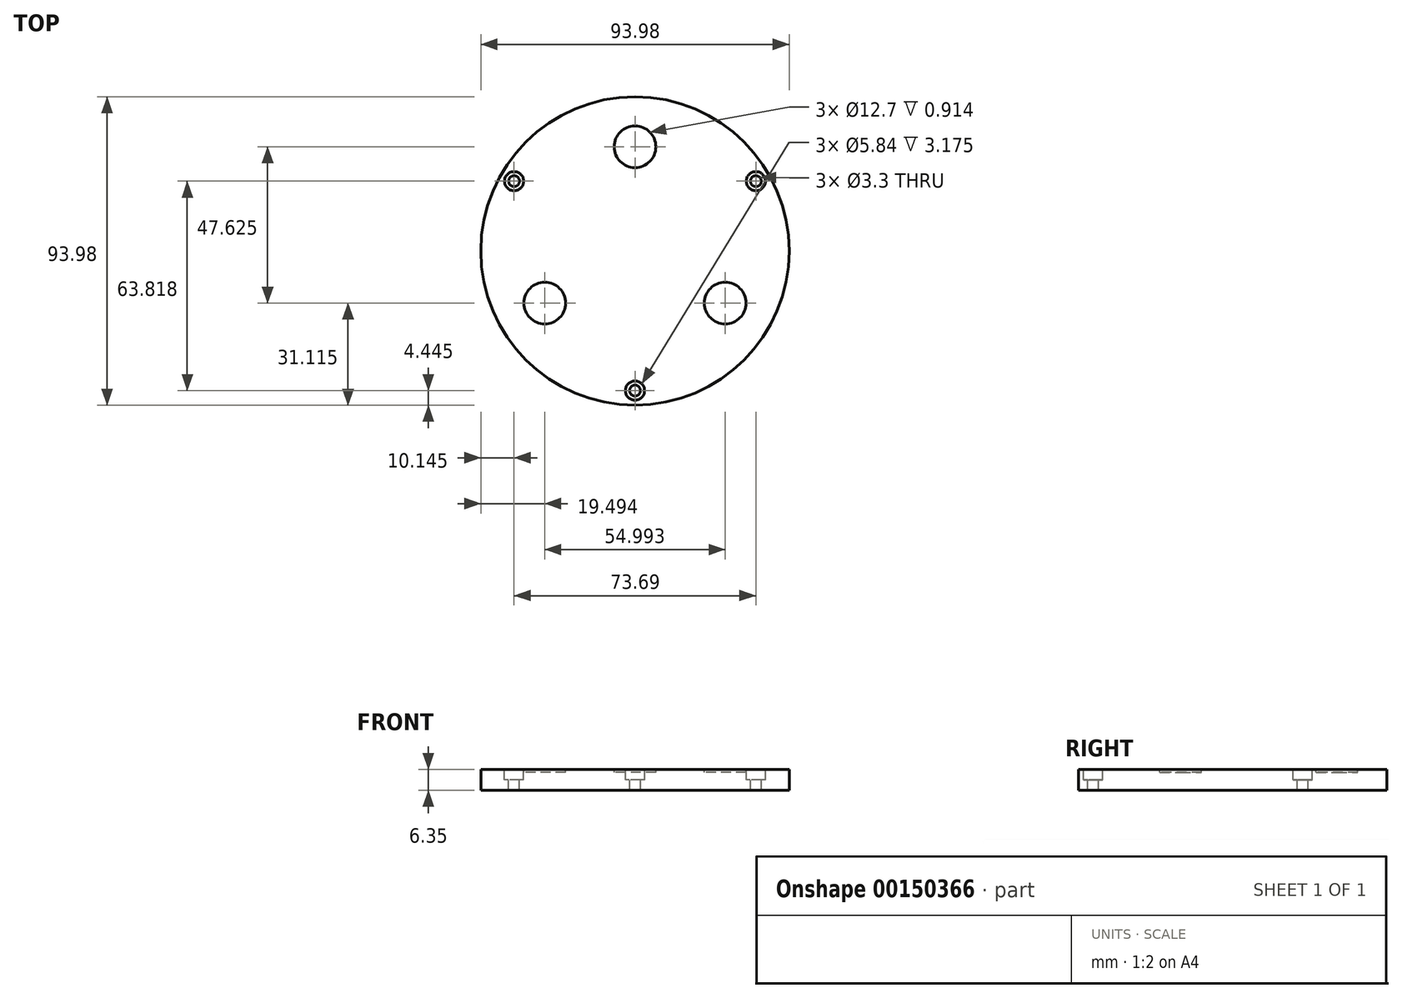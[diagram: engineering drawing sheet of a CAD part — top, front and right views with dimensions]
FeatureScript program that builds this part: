
annotation { "Feature Type Name" : "Feature", "Feature Type Description" : "" }
export const myFeature = defineFeature(function(context is Context, id is Id, definition is map)
    precondition{}
    {
        {
            var Q0;
            Q0=qCreatedBy(makeId("Top.planeOp"),FACE);
            var sketch = newSketch(context, id + "F0", { "sketchPlane" : qUnion([Q0])});
            skCircle(sketch, "E0", {"center": v(0, 0) * mm, "radius": 47 * mm});
            skSolve(sketch);
        }
        {
            var Q0;
            Q0 = qSketchRegion(id + "F0", true);
            extrude(context, id + "F1", {"entities" : qUnion([Q0]), "depth" : 6.35 * mm});
        }
        {
            var Q0;
            Q0=makeQuery(id+"F1.opExtrude","CAP_FACE",FACE,{"disambiguationData":[OSD([sQuery(id+"F0.wireOp",EDGE,"E0")])],"isStart":false});
            var sketch = newSketch(context, id + "F2", { "sketchPlane" : qUnion([Q0])});
            skCircle(sketch, "E1", {"center": v(0, 31.75) * mm, "radius": 6.35 * mm});
            skCircle(sketch, "E2", {"center": v(-27.5, -15.88) * mm, "radius": 6.35 * mm});
            skCircle(sketch, "E3", {"center": v(27.5, -15.88) * mm, "radius": 6.35 * mm});
            skLineSegment(sketch, "E4", {"start": v(0, 31.75) * mm, "end": v(-27.5, -15.88) * mm, "construction": true});
            skLineSegment(sketch, "E5", {"start": v(27.5, -15.88) * mm, "end": v(0, 31.75) * mm, "construction": true});
            skLineSegment(sketch, "E6", {"start": v(27.5, -15.88) * mm, "end": v(-27.5, -15.88) * mm, "construction": true});
            skLineSegment(sketch, "E7", {"start": v(-13.75, 7.94) * mm, "end": v(0, 0) * mm, "construction": true});
            skLineSegment(sketch, "E8", {"start": v(0, 0) * mm, "end": v(0, -15.88) * mm, "construction": true});
            skSolve(sketch);
        }
        {
            var Q0;
            Q0 = qSketchRegion(id + "F2", true);
            extrude(context, id + "F3", {"entities" : qUnion([Q0]), "operationType" : NewBodyOperationType.REMOVE, "oppositeDirection" : true, "depth" : 0.91 * mm});
        }
        {
            var Q0;
            Q0=makeQuery(id+"F1.opExtrude","CAP_FACE",FACE,{"disambiguationData":[OSD([sQuery(id+"F0.wireOp",EDGE,"E0")])],"isStart":false});
            var sketch = newSketch(context, id + "F4", { "sketchPlane" : qUnion([Q0])});
            skCircle(sketch, "E9", {"center": v(0, -42.55) * mm, "radius": 2.92 * mm});
            skCircle(sketch, "E10", {"center": v(-36.85, 21.27) * mm, "radius": 2.92 * mm});
            skCircle(sketch, "E11", {"center": v(36.85, 21.27) * mm, "radius": 2.92 * mm});
            skCircle(sketch, "E12", {"center": v(0, 0) * mm, "radius": 42.55 * mm, "construction": true});
            skLineSegment(sketch, "E13", {"start": v(0, -42.55) * mm, "end": v(-36.85, 21.27) * mm, "construction": true});
            skLineSegment(sketch, "E14", {"start": v(36.85, 21.27) * mm, "end": v(0, -42.55) * mm, "construction": true});
            skLineSegment(sketch, "E15", {"start": v(-36.85, 21.27) * mm, "end": v(36.85, 21.27) * mm, "construction": true});
            skSolve(sketch);
        }
        {
            var Q0;
            Q0 = qSketchRegion(id + "F4", true);
            extrude(context, id + "F5", {"entities" : qUnion([Q0]), "operationType" : NewBodyOperationType.REMOVE, "oppositeDirection" : true, "depth" : 3.17 * mm});
        }
        {
            var Q0;
            Q0=makeQuery(id+"F1.opExtrude","CAP_FACE",FACE,{"disambiguationData":[OSD([sQuery(id+"F0.wireOp",EDGE,"E0")])],"isStart":false});
            var sketch = newSketch(context, id + "F6", { "sketchPlane" : qUnion([Q0])});
            skCircle(sketch, "E16", {"center": v(-36.85, 21.27) * mm, "radius": 1.65 * mm});
            skCircle(sketch, "E17", {"center": v(36.85, 21.27) * mm, "radius": 1.65 * mm});
            skCircle(sketch, "E18", {"center": v(0, -42.55) * mm, "radius": 1.65 * mm});
            skSolve(sketch);
        }
        {
            var Q0;
            Q0 = qSketchRegion(id + "F6", true);
            extrude(context, id + "F7", {"entities" : qUnion([Q0]), "operationType" : NewBodyOperationType.REMOVE, "oppositeDirection" : true, "depth" : 25.4 * mm});
        }
    });
